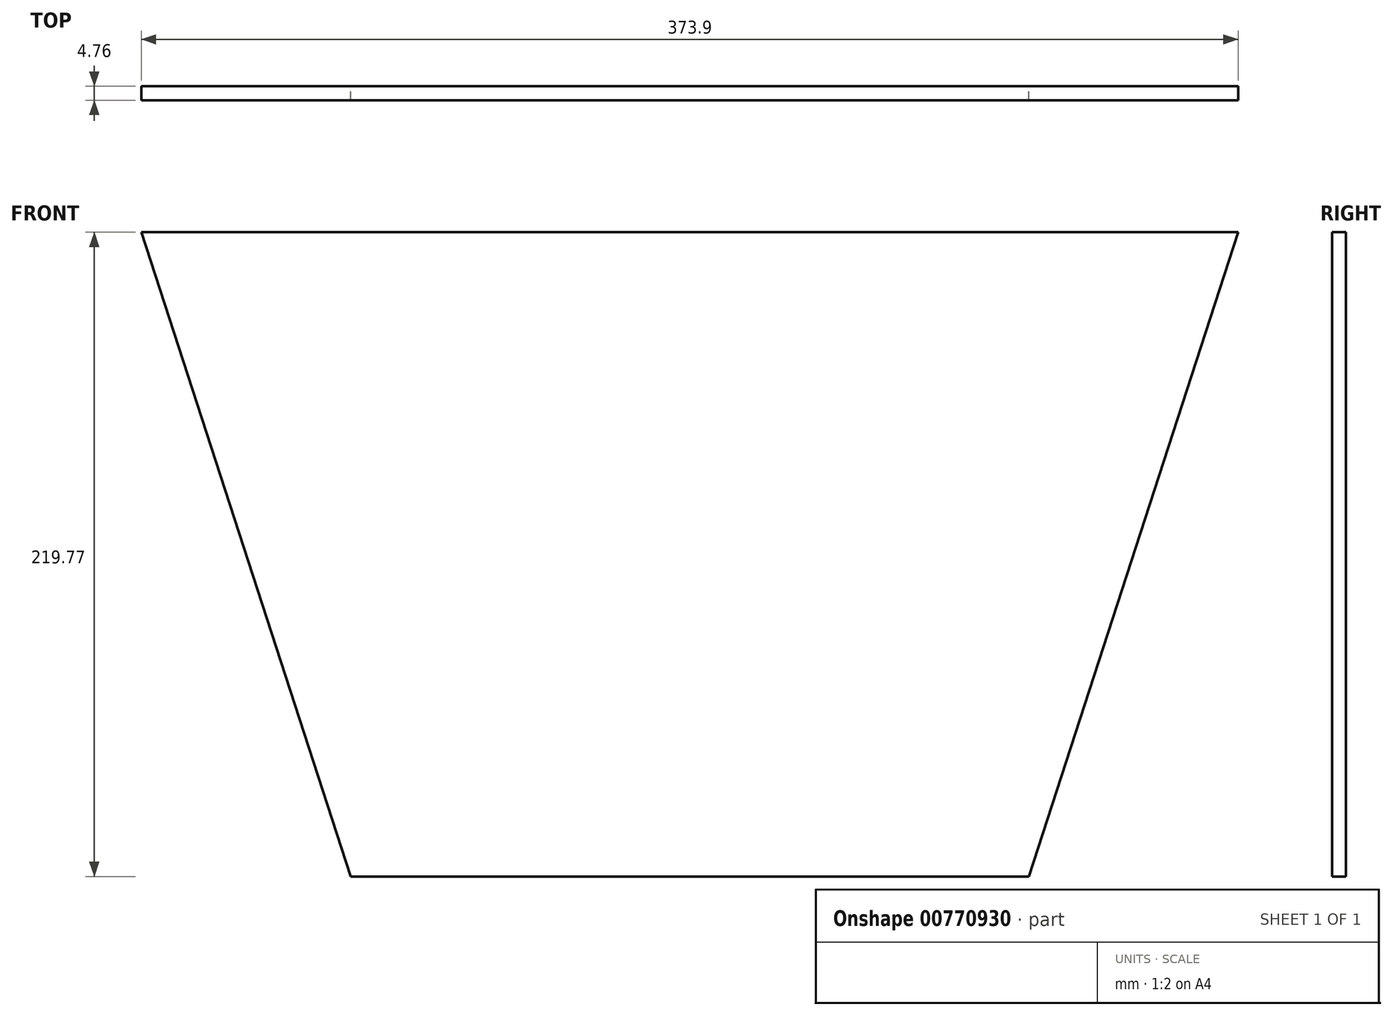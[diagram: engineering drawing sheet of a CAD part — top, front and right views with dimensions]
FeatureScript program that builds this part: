
annotation { "Feature Type Name" : "Feature", "Feature Type Description" : "" }
export const myFeature = defineFeature(function(context is Context, id is Id, definition is map)
    precondition{}
    {
        {
            var Q0;
            Q0=qCreatedBy(makeId("Front.planeOp"),FACE);
            var sketch = newSketch(context, id + "F0", { "sketchPlane" : qUnion([Q0])});
            skCircle(sketch, "E0.cCircle", {"center": v(0, 0) * mm, "radius": 159.03 * mm, "construction": true});
            skLineSegment(sketch, "E0.0", {"start": v(115.54, -159.03) * mm, "end": v(-115.54, -159.03) * mm});
            skLineSegment(sketch, "E0.1", {"start": v(-115.54, -159.03) * mm, "end": v(-186.95, 60.74) * mm});
            skLineSegment(sketch, "E0.4", {"start": v(186.95, 60.74) * mm, "end": v(115.54, -159.03) * mm});
            skPoint(sketch, "E0.0.midPoint", {"position": v(0, -159.03) * mm});
            skLineSegment(sketch, "E1", {"start": v(-186.95, 60.74) * mm, "end": v(186.95, 60.74) * mm});
            skSolve(sketch);
        }
        {
            var Q0;
            Q0=makeQuery(id+"F0.imprint","IMPRINT",FACE,{"disambiguationData":[TD([[makeQuery(id+"F0.imprint","IMPRINT",EDGE,{"derivedFrom":sQuery(id+"F0.wireOp",EDGE,"E0.0")}),-1.0]])]});
            extrude(context, id + "F1", {"entities" : qUnion([Q0]), "endBound" : BoundingType.SYMMETRIC, "depth" : 4.76 * mm, "offsetDistance" : 25.4 * mm});
        }
    });
